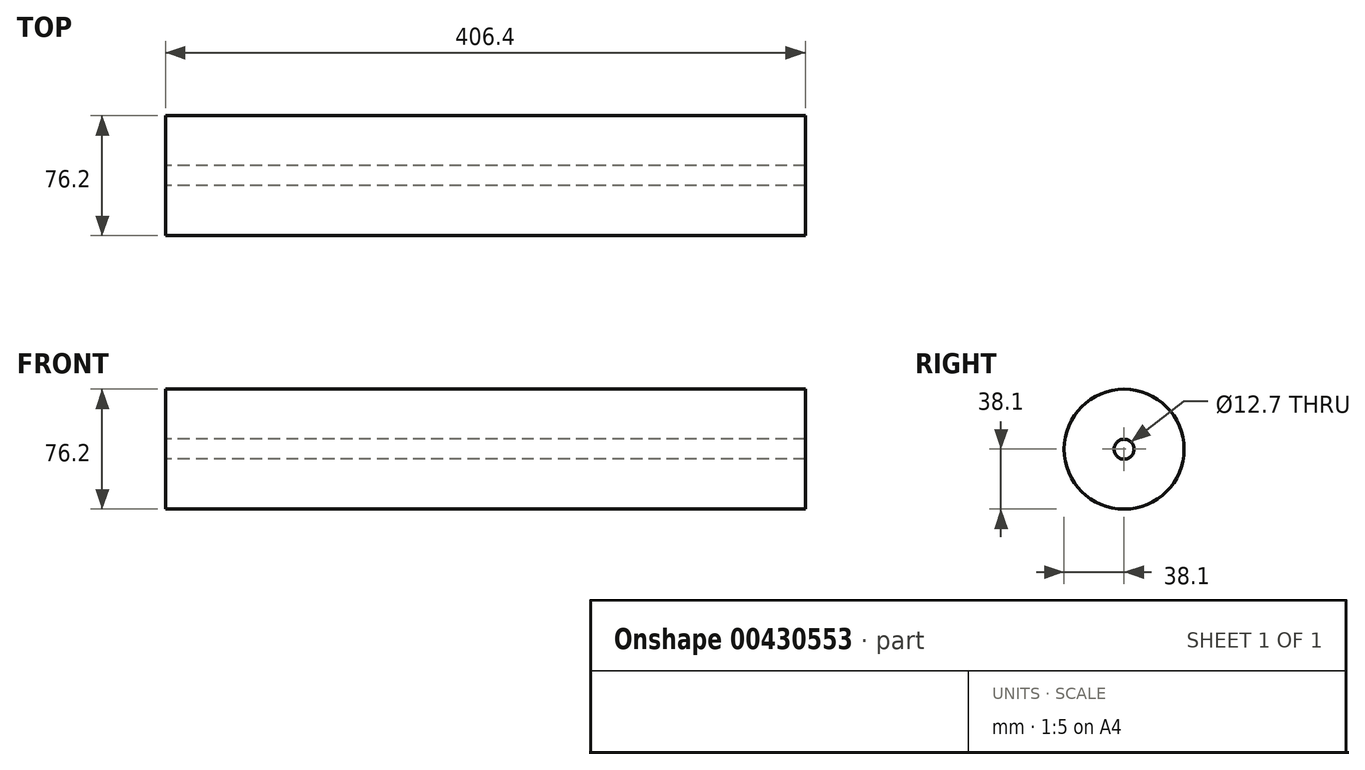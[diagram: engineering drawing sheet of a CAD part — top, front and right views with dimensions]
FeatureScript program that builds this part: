
annotation { "Feature Type Name" : "Feature", "Feature Type Description" : "" }
export const myFeature = defineFeature(function(context is Context, id is Id, definition is map)
    precondition{}
    {
        {
            var Q0;
            Q0=qCreatedBy(makeId("Right.planeOp"),FACE);
            var sketch = newSketch(context, id + "F0", { "sketchPlane" : qUnion([Q0])});
            skCircle(sketch, "E0", {"center": v(0, 0) * mm, "radius": 38.1 * mm});
            skCircle(sketch, "E1", {"center": v(0, 0) * mm, "radius": 6.35 * mm});
            skSolve(sketch);
        }
        {
            var Q0;
            Q0=makeQuery(id+"F0.imprint","IMPRINT",FACE,{"disambiguationData":[TD([[makeQuery(id+"F0.imprint","IMPRINT",EDGE,{"derivedFrom":sQuery(id+"F0.wireOp",EDGE,"E0")}),1.0]])]});
            extrude(context, id + "F1", {"entities" : qUnion([Q0]), "depth" : 406.4 * mm});
        }
    });
